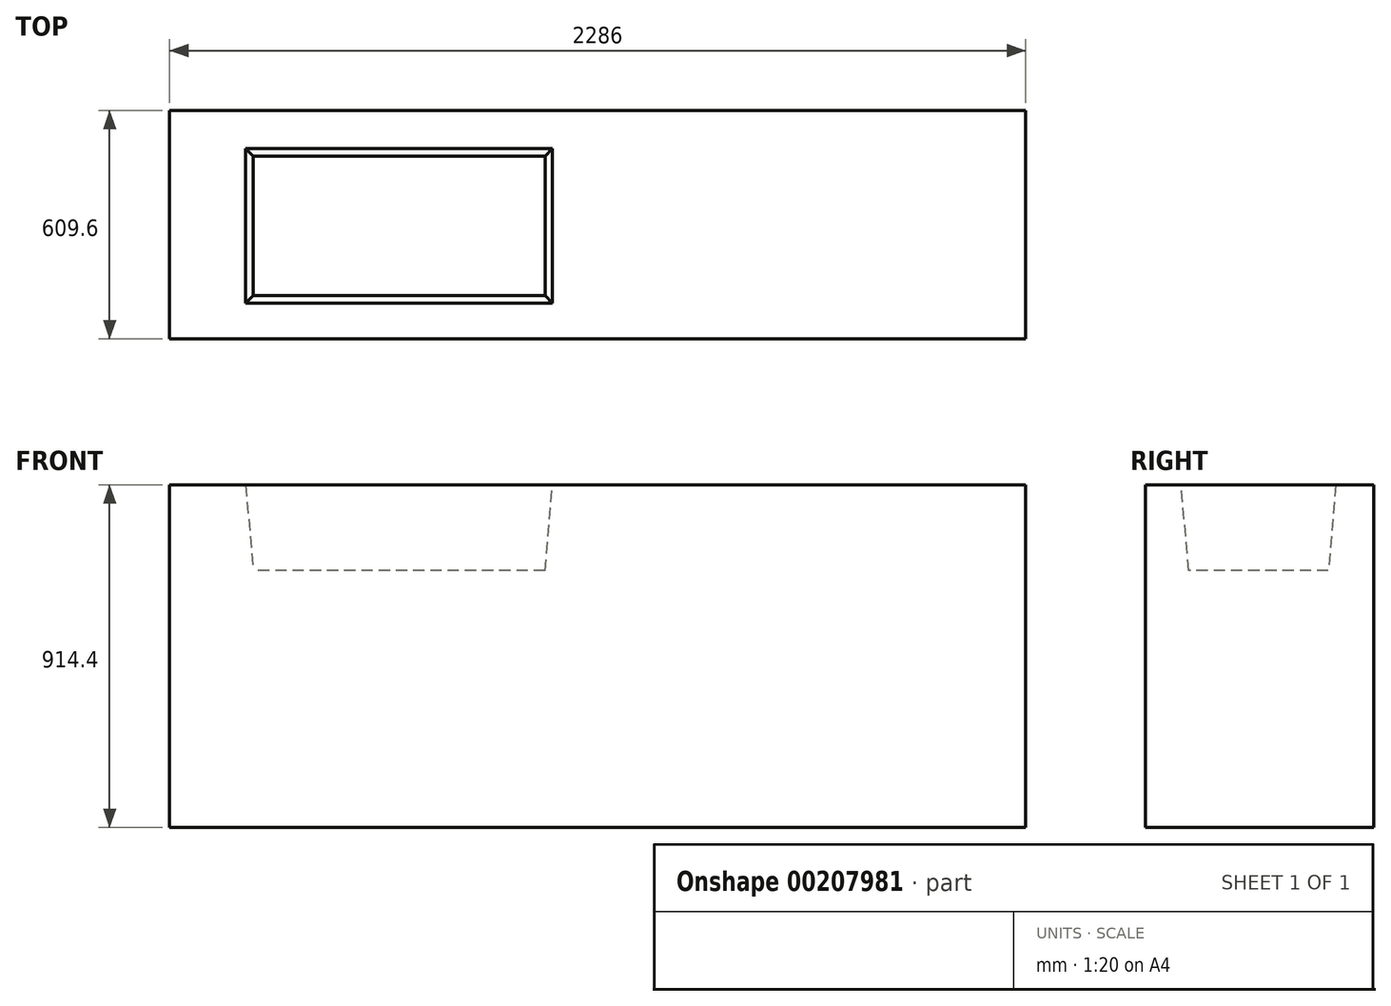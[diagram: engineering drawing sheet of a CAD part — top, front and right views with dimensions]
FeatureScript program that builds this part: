
annotation { "Feature Type Name" : "Feature", "Feature Type Description" : "" }
export const myFeature = defineFeature(function(context is Context, id is Id, definition is map)
    precondition{}
    {
        {
            var Q0;
            Q0=qCreatedBy(makeId("Top.planeOp"),FACE);
            var sketch = newSketch(context, id + "F0", { "sketchPlane" : qUnion([Q0])});
            skLineSegment(sketch, "E0.bottom", {"start": v(0, 0) * mm, "end": v(-2286, 0) * mm});
            skLineSegment(sketch, "E0.top", {"start": v(0, -609.6) * mm, "end": v(-2286, -609.6) * mm});
            skLineSegment(sketch, "E0.left", {"start": v(0, 0) * mm, "end": v(0, -609.6) * mm});
            skLineSegment(sketch, "E0.right", {"start": v(-2286, 0) * mm, "end": v(-2286, -609.6) * mm});
            skSolve(sketch);
        }
        {
            var Q0;
            Q0=makeQuery(id+"F0.imprint","IMPRINT",FACE,{"disambiguationData":[TD([[makeQuery(id+"F0.imprint","IMPRINT",EDGE,{"derivedFrom":sQuery(id+"F0.wireOp",EDGE,"E0.bottom")}),1.0]])]});
            extrude(context, id + "F1", {"entities" : qUnion([Q0]), "depth" : 914.4 * mm});
        }
        {
            var Q0;
            Q0=makeQuery(id+"F1.opExtrude","CAP_FACE",FACE,{"disambiguationData":[OSD([sQuery(id+"F0.wireOp",EDGE,"E0.bottom"),sQuery(id+"F0.wireOp",EDGE,"E0.top"),sQuery(id+"F0.wireOp",EDGE,"E0.left"),sQuery(id+"F0.wireOp",EDGE,"E0.right")])],"isStart":false});
            var sketch = newSketch(context, id + "F2", { "sketchPlane" : qUnion([Q0])});
            skLineSegment(sketch, "E1.bottom", {"start": v(-2082.8, -101.6) * mm, "end": v(-1263.65, -101.6) * mm});
            skLineSegment(sketch, "E1.top", {"start": v(-2082.8, -514.35) * mm, "end": v(-1263.65, -514.35) * mm});
            skLineSegment(sketch, "E1.left", {"start": v(-2082.8, -101.6) * mm, "end": v(-2082.8, -514.35) * mm});
            skLineSegment(sketch, "E1.right", {"start": v(-1263.65, -101.6) * mm, "end": v(-1263.65, -514.35) * mm});
            skSolve(sketch);
        }
        {
            var Q0;
            Q0=makeQuery(id+"F2.imprint","IMPRINT",FACE,{"disambiguationData":[TD([[makeQuery(id+"F2.imprint","IMPRINT",EDGE,{"derivedFrom":sQuery(id+"F2.wireOp",EDGE,"E1.bottom")}),-1.0]])]});
            extrude(context, id + "F3", {"entities" : qUnion([Q0]), "operationType" : NewBodyOperationType.REMOVE, "oppositeDirection" : true, "depth" : 228.6 * mm, "hasDraft" : true, "draftAngle" : 5 * degree, "draftPullDirection" : true});
        }
    });
